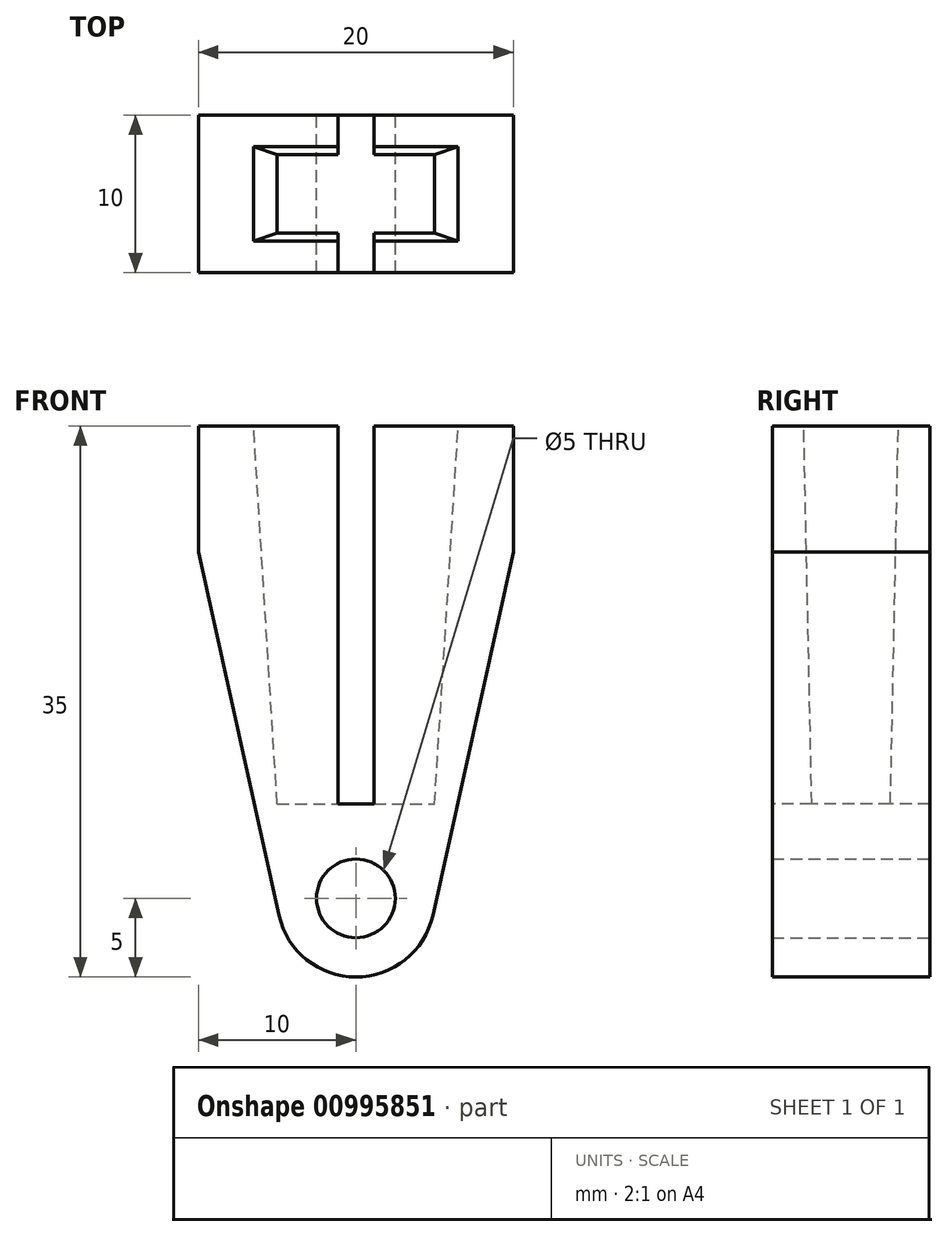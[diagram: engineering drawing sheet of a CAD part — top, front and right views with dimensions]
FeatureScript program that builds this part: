
annotation { "Feature Type Name" : "Feature", "Feature Type Description" : "" }
export const myFeature = defineFeature(function(context is Context, id is Id, definition is map)
    precondition{}
    {
        {
            var Q0;
            Q0=qCreatedBy(makeId("Front.planeOp"),FACE);
            var sketch = newSketch(context, id + "F0", { "sketchPlane" : qUnion([Q0])});
            skArc(sketch, "E0", {"start": v(4.88, -1.08) * mm, "mid": v(0, -5) * mm, "end": v(-4.88, -1.08) * mm});
            skLineSegment(sketch, "E1", {"start": v(-4.88, -1.08) * mm, "end": v(-10, 22) * mm});
            skLineSegment(sketch, "E2", {"start": v(10, 22) * mm, "end": v(4.88, -1.08) * mm});
            skCircle(sketch, "E3", {"center": v(0, 0) * mm, "radius": 2.5 * mm});
            skLineSegment(sketch, "E4", {"start": v(-10, 22) * mm, "end": v(-10, 30) * mm});
            skLineSegment(sketch, "E5", {"start": v(-10, 30) * mm, "end": v(10, 30) * mm});
            skLineSegment(sketch, "E6", {"start": v(10, 30) * mm, "end": v(10, 22) * mm});
            skSolve(sketch);
        }
        {
            var Q0;
            Q0 = qSketchRegion(id + "F0", true);
            extrude(context, id + "F1", {"entities" : qUnion([Q0]), "endBound" : BoundingType.SYMMETRIC, "depth" : 10 * mm, "offsetDistance" : 25 * mm});
        }
        {
            var Q0;
            Q0=makeQuery(id+"F1.opExtrude","SWEPT_FACE",FACE,{"disambiguationData":[OSD([sQuery(id+"F0.wireOp",EDGE,"E5")])]});
            var sketch = newSketch(context, id + "F2", { "sketchPlane" : qUnion([Q0])});
            skLineSegment(sketch, "E7.bottom", {"start": v(-1.15, 5) * mm, "end": v(1.15, 5) * mm});
            skLineSegment(sketch, "E7.top", {"start": v(-1.15, -5) * mm, "end": v(1.15, -5) * mm});
            skLineSegment(sketch, "E7.left", {"start": v(-1.15, 5) * mm, "end": v(-1.15, -5) * mm});
            skLineSegment(sketch, "E7.right", {"start": v(1.15, 5) * mm, "end": v(1.15, -5) * mm});
            skSolve(sketch);
        }
        {
            var Q0;
            Q0 = qSketchRegion(id + "F2", true);
            extrude(context, id + "F3", {"entities" : qUnion([Q0]), "operationType" : NewBodyOperationType.REMOVE, "oppositeDirection" : true, "depth" : (22 + 8 - 6) * mm, "offsetDistance" : 25 * mm});
        }
        {
            var Q0;
            Q0=qCreatedBy(makeId("Top.planeOp"),FACE);
            cPlane(context, id + "F4", {"entities" : qUnion([Q0]), "cplaneType" : CPlaneType.OFFSET, "offset" : 6 * mm, "width" : 150 * mm, "height" : 150 * mm});
        }
        {
            var Q0;
            Q0=qCreatedBy(id+"F4.planeOp",FACE);
            var sketch = newSketch(context, id + "F5", { "sketchPlane" : qUnion([Q0])});
            skLineSegment(sketch, "E8.bottom", {"start": v(-5, 2.5) * mm, "end": v(5, 2.5) * mm});
            skLineSegment(sketch, "E8.top", {"start": v(-5, -2.5) * mm, "end": v(5, -2.5) * mm});
            skLineSegment(sketch, "E8.left", {"start": v(-5, 2.5) * mm, "end": v(-5, -2.5) * mm});
            skLineSegment(sketch, "E8.right", {"start": v(5, 2.5) * mm, "end": v(5, -2.5) * mm});
            skSolve(sketch);
        }
        {
            var Q0;
            Q0=qCreatedBy(makeId("Top.planeOp"),FACE);
            cPlane(context, id + "F6", {"entities" : qUnion([Q0]), "cplaneType" : CPlaneType.OFFSET, "offset" : 30 * mm, "width" : 150 * mm, "height" : 150 * mm});
        }
        {
            var Q0;
            Q0=qCreatedBy(id+"F6.planeOp",FACE);
            var sketch = newSketch(context, id + "F7", { "sketchPlane" : qUnion([Q0])});
            skLineSegment(sketch, "E9.bottom", {"start": v(-6.5, 3) * mm, "end": v(6.5, 3) * mm});
            skLineSegment(sketch, "E9.top", {"start": v(-6.5, -3) * mm, "end": v(6.5, -3) * mm});
            skLineSegment(sketch, "E9.left", {"start": v(-6.5, 3) * mm, "end": v(-6.5, -3) * mm});
            skLineSegment(sketch, "E9.right", {"start": v(6.5, 3) * mm, "end": v(6.5, -3) * mm});
            skSolve(sketch);
        }
        {
            var Q1;
            Q1 = qSketchRegion(id + "F5", true);
            var Q2;
            Q2 = qSketchRegion(id + "F7", true);
            loft(context, id + "F8", {"operationType" : NewBodyOperationType.REMOVE, "sheetProfilesArray" : [{ "sheetProfileEntities" : qUnion([Q1]) }, { "sheetProfileEntities" : qUnion([Q2]) }]});
        }
    });
